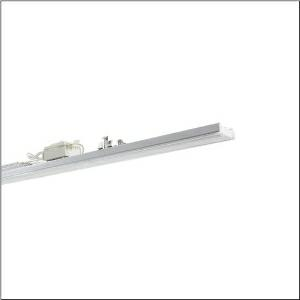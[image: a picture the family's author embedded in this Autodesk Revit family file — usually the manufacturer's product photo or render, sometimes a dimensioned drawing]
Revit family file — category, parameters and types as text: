
# Revit family: licross_21_recessed_mo_52tl19mn4a5g
name_source: partatom
category: Lighting Fixtures
units: mm (PartAtom-declared; Revit-internal decimal feet)

## family parameters
Cut with Voids When Loaded = No
Host = Face
Light Source = No
Part Type = Normal
Room Calculation Point = No
Round Connector Dimension = Use Diameter
Shared = No

## types (1)
- --- (1 x LED, 10530 lm, 60.5 W, 4000K)
    Apparent Load = 61 VA
    CIE Flux Codes = 55 90 98 100 100
    Color Rendering = 80
    Color Temperature = 4000K
    Default Elevation = 1800 mm
    Description = Licross 21 Recessed MO, luminaire insert, of sheet steel, galvanised, coil coated, white, length: 1.500mm, width: 66mm, height: 67mm, LED rated luminous flux: 10.530lm, light colour: 840, SDCM (Standard Deviation of Colour Matching)MacAdam ≤ 3 SDCM (initial), control gear: ON/OFF Multilumen, with plug, 3-pole, with phase selection, mains connection: 220..240V, AC, 50/60Hz, rated input power: 61W, internal wiring halogen-free, primary light control with lens, of plastic, primary optical cover: cover, of PMMA, light emission: direct distribution, primary light characteristic: double asymmetric, protection rating (complete): IP40, insulation class (complete): insulation class I (protective earthing), certification: CE, ENEC, VDE, UKCA, protection symbol: D if used in an environment without relevant dust loads with corresponding accessories, impact resistance: IK06, permissible ambient temperature for indoor applications: -35..+40°C, corresponds to IFS (International Featured Standards) requirements for safety and quality in the food industry, reducing of maximum allowable ambient temperature of 5°C with ceiling mounting, LABS conformity tested according to VDMA 24364:2018-05, The light source and the operating device comply with the requirements of the Ecodesign Regulation (EU) 2019/2020 and are replaceable in accordance with this regulation, packaging unit: 1 piece
    Height = 58 mm
    Lamp = 1 x LED
    Lamp Light Flux = 10530 lm
    Lamp Power = 60.5 W
    Lamp count = 1
    Length = 1500 mm
    Luminous efficacy = 174 lm/W
    Manufacturer = Siteco
    ModVariant = No
    Model = 52TL19MN4A5G
    Mounting Place = Ceiling
    Mounting Type = Pendant
    Number of Poles = 1
    OnlyDefault = Yes
    Power Factor = 1
    Product Name = Licross 21 Recessed MO
    Product group = luminaire insert | ceiling pendant
    ProductGroupID = 901
    Protection Class = Protection class I
    Protection Degree = IP 40
    RLX_Detail_Level = 1
    RLX_Emergency_Light_Flux = 0 lm
    RLX_Emergency_Type = 0
    RLX_Emergency_Type_DB = No
    RlxData = <blob elided: 22529 chars, md5=bab280e3>
    Socket = socket
    Standby Power = 0 W
    System Light Flux = 10530 lm
    System Power = 61 W
    Type Comments = factory setting: luminous flux: 100 % | (A | C | E) | 140 mA
    Type Image = l_1296930.jpg
    URL = http://relux.com
    VarID = @adj_108959
    Voltage = 0 V
    Weight = 0.00 kg
    Width = 66 mm

## geometry (parser evidence)
native form markers: Blend x4, Sweep x12
no freeform markers — native parametric forms only
